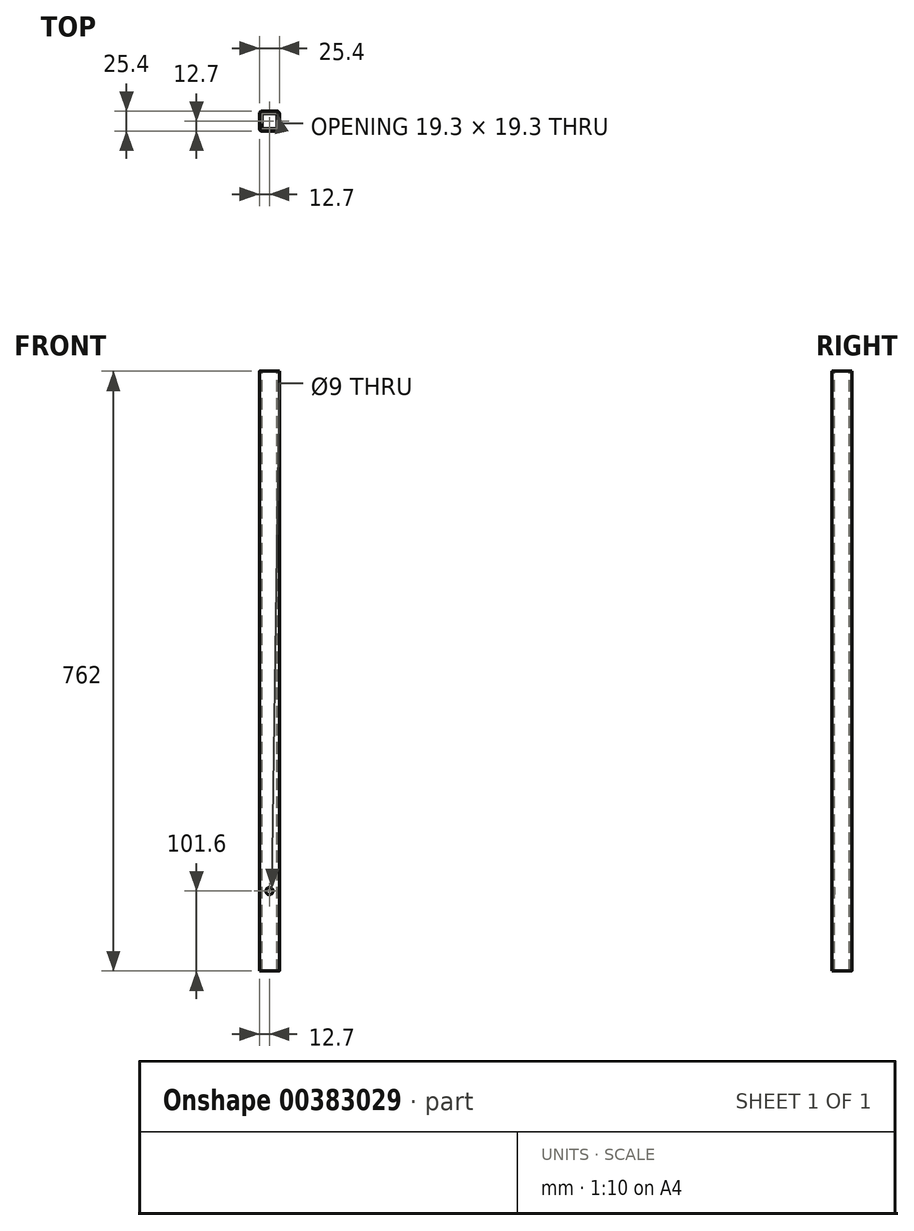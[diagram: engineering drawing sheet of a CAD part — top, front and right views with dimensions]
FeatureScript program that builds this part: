
annotation { "Feature Type Name" : "Feature", "Feature Type Description" : "" }
export const myFeature = defineFeature(function(context is Context, id is Id, definition is map)
    precondition{}
    {
        {
            var Q0;
            Q0=qCreatedBy(makeId("Top.planeOp"),FACE);
            var sketch = newSketch(context, id + "F0", { "sketchPlane" : qUnion([Q0])});
            skLineSegment(sketch, "E0.bottom", {"start": v(12.7, 12.7) * mm, "end": v(-12.7, 12.7) * mm});
            skLineSegment(sketch, "E0.top", {"start": v(12.7, -12.7) * mm, "end": v(-12.7, -12.7) * mm});
            skLineSegment(sketch, "E0.left", {"start": v(12.7, 12.7) * mm, "end": v(12.7, -12.7) * mm});
            skLineSegment(sketch, "E0.right", {"start": v(-12.7, 12.7) * mm, "end": v(-12.7, -12.7) * mm});
            skPoint(sketch, "E0.middle", {"position": v(0, 0) * mm});
            skSolve(sketch);
        }
        {
            var Q0;
            Q0=qSketchRegion(id+"F0",true);
            extrude(context, id + "F1", {"entities" : qUnion([Q0]), "oppositeDirection" : true, "depth" : 762 * mm});
        }
        {
            var Q0;
            Q0=makeQuery(id+"F1.opExtrude","SWEPT_EDGE",EDGE,{"disambiguationData":[OSD([sQuery(id+"F0.wireOp",EDGE,"E0.bottom"),sQuery(id+"F0.wireOp",EDGE,"E0.right")])]});
            var Q1;
            Q1=makeQuery(id+"F1.opExtrude","SWEPT_EDGE",EDGE,{"disambiguationData":[OSD([sQuery(id+"F0.wireOp",EDGE,"E0.top"),sQuery(id+"F0.wireOp",EDGE,"E0.right")])]});
            var Q2;
            Q2=makeQuery(id+"F1.opExtrude","SWEPT_EDGE",EDGE,{"disambiguationData":[OSD([sQuery(id+"F0.wireOp",EDGE,"E0.bottom"),sQuery(id+"F0.wireOp",EDGE,"E0.left")])]});
            var Q3;
            Q3=makeQuery(id+"F1.opExtrude","SWEPT_EDGE",EDGE,{"disambiguationData":[OSD([sQuery(id+"F0.wireOp",EDGE,"E0.top"),sQuery(id+"F0.wireOp",EDGE,"E0.left")])]});
            fillet(context, id + "F2", {"entities" : qUnion([Q0, Q1, Q2, Q3]), "radius" : 3.17 * mm, "tangentPropagation" : true, "allowEdgeOverflow" : false});
        }
        {
            var Q0;
            Q0=makeQuery(id+"F1.opExtrude","CAP_FACE",FACE,{"disambiguationData":[OSD([sQuery(id+"F0.wireOp",EDGE,"E0.bottom"),sQuery(id+"F0.wireOp",EDGE,"E0.top"),sQuery(id+"F0.wireOp",EDGE,"E0.left"),sQuery(id+"F0.wireOp",EDGE,"E0.right")])],"isStart":true});
            var Q1;
            Q1=makeQuery(id+"F1.opExtrude","CAP_FACE",FACE,{"disambiguationData":[OSD([sQuery(id+"F0.wireOp",EDGE,"E0.bottom"),sQuery(id+"F0.wireOp",EDGE,"E0.top"),sQuery(id+"F0.wireOp",EDGE,"E0.left"),sQuery(id+"F0.wireOp",EDGE,"E0.right")])],"isStart":false});
            shell(context, id + "F3", {"entities" : qUnion([Q0, Q1]), "thickness" : 3.05 * mm});
        }
        {
            var Q0;
            Q0=qCreatedBy(makeId("Front.planeOp"),FACE);
            var sketch = newSketch(context, id + "F4", { "sketchPlane" : qUnion([Q0])});
            skCircle(sketch, "E1", {"center": v(0, -660.4) * mm, "radius": 4.5 * mm});
            skSolve(sketch);
        }
        {
            var Q0;
            Q0=qSketchRegion(id+"F4",true);
            var Q1;
            Q1=makeQuery(id+"F1.opExtrude","SWEPT_FACE",FACE,{"disambiguationData":[OSD([sQuery(id+"F0.wireOp",EDGE,"E0.top")])]});
            extrude(context, id + "F5", {"entities" : qUnion([Q0]), "operationType" : NewBodyOperationType.REMOVE, "endBound" : BoundingType.UP_TO_SURFACE, "endBoundEntityFace" : qUnion([Q1]), "depth" : 25.4 * mm});
        }
    });
